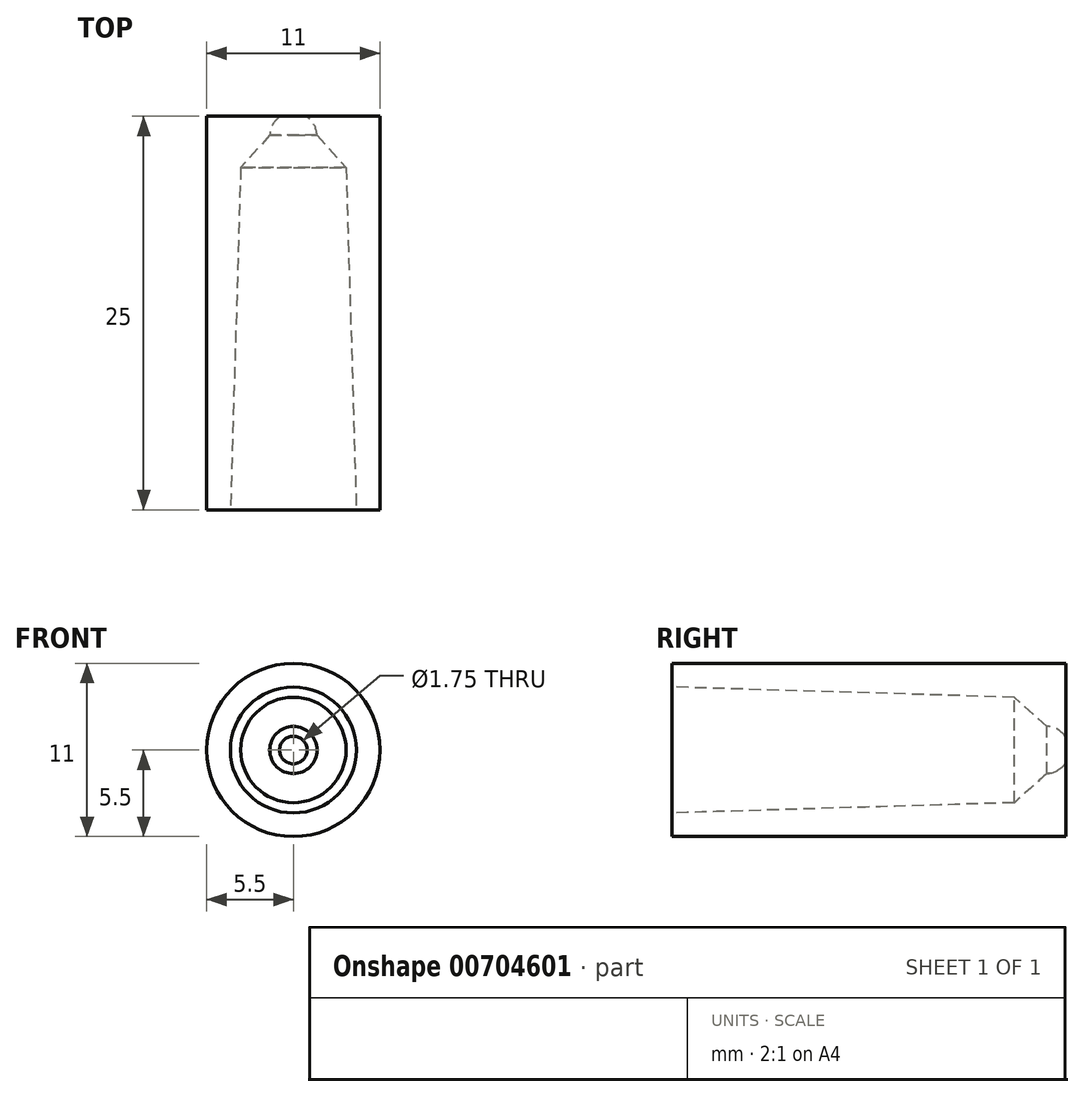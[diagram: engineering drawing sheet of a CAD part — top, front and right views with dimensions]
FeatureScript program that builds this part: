
annotation { "Feature Type Name" : "Feature", "Feature Type Description" : "" }
export const myFeature = defineFeature(function(context is Context, id is Id, definition is map)
    precondition{}
    {
        {
            var Q0;
            Q0=qCreatedBy(makeId("Right.planeOp"),FACE);
            var sketch = newSketch(context, id + "F0", { "sketchPlane" : qUnion([Q0])});
            skLineSegment(sketch, "E0", {"start": v(0, 0) * mm, "end": v(0, 0.88) * mm, "construction": true});
            skLineSegment(sketch, "E1", {"start": v(0, 0.88) * mm, "end": v(-0.03, 0.88) * mm});
            skLineSegment(sketch, "E2", {"start": v(-25, 5.5) * mm, "end": v(0, 5.5) * mm});
            skLineSegment(sketch, "E3", {"start": v(0, 5.5) * mm, "end": v(0, 0.88) * mm});
            skLineSegment(sketch, "E4", {"start": v(-25, 0) * mm, "end": v(0, 0) * mm, "construction": true});
            skPoint(sketch, "E5.visualSharp", {"position": v(61.5, -5.1) * mm});
            skArc(sketch, "E6.trimOffspring", {"start": v(-0.03, 0.87) * mm, "mid": v(-0.55, 1.32) * mm, "end": v(-1.2, 1.5) * mm});
            skPoint(sketch, "E7.filletArc.center.orphan", {"position": v(-2.75, 0) * mm});
            skLineSegment(sketch, "E8", {"start": v(-1.2, 1.5) * mm, "end": v(-3.27, 3.35) * mm});
            skPoint(sketch, "E9.start.orphan", {"position": v(-25, 4) * mm});
            skLineSegment(sketch, "E10", {"start": v(-3.27, 3.35) * mm, "end": v(-25, 4) * mm});
            skLineSegment(sketch, "E11", {"start": v(-25, 5.5) * mm, "end": v(-25, 4) * mm});
            skSolve(sketch);
        }
        {
            var Q0;
            Q0 = qSketchRegion(id + "F0", true);
            var Q1;
            Q1=sQuery(id+"F0.wireOp",EDGE,"E4");
            revolve(context, id + "F1", {"surfaceOperationType" : NewSurfaceOperationType.NEW, "entities" : qUnion([Q0]), "axis" : qUnion([Q1]), "revolveType" : RevolveType.FULL});
        }
    });
